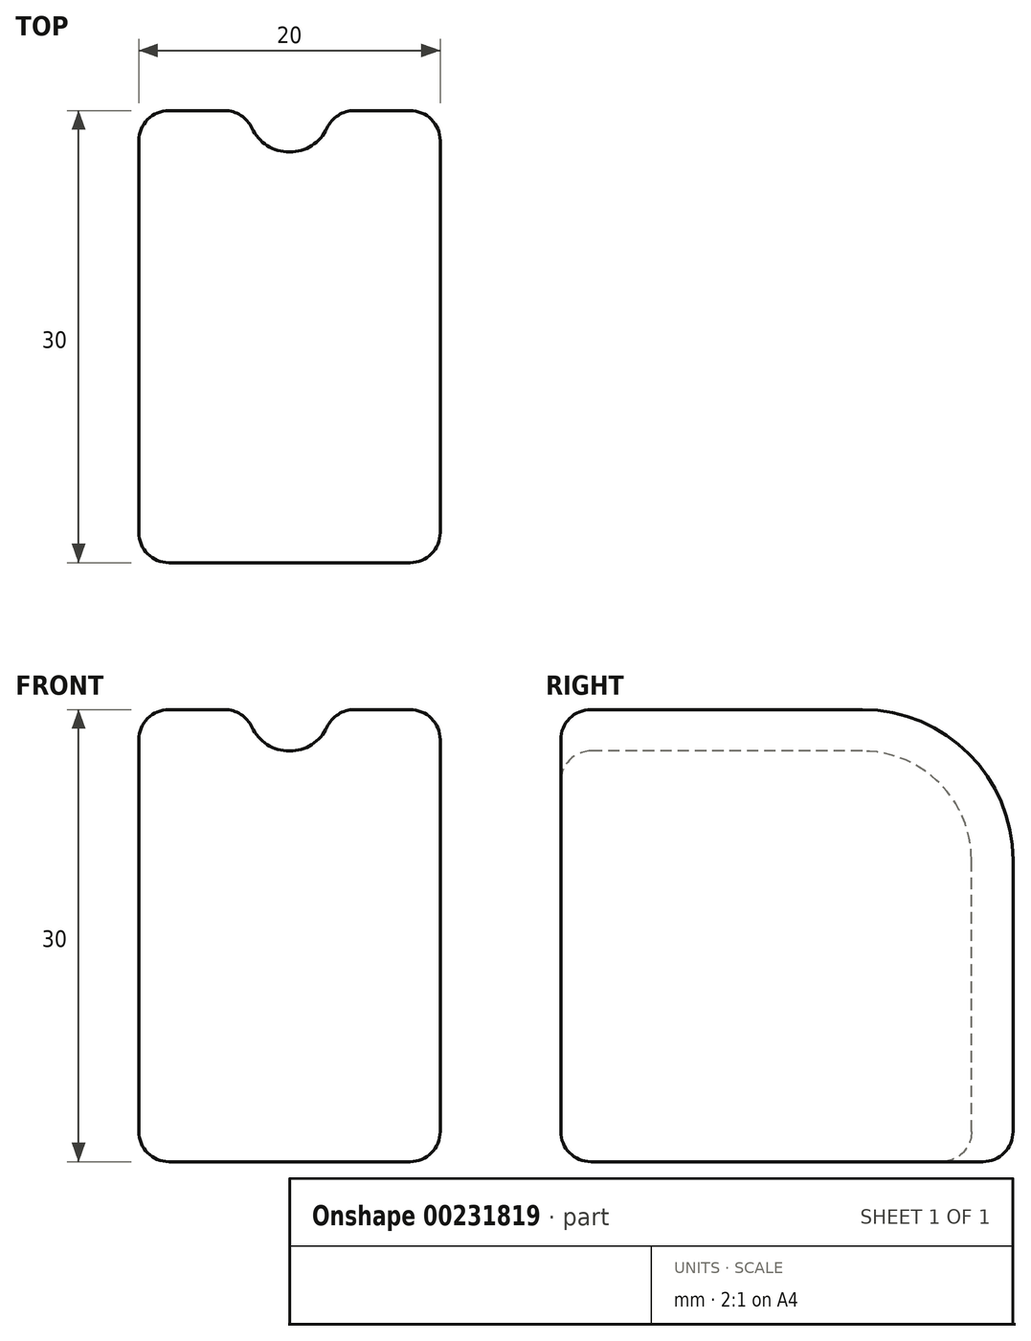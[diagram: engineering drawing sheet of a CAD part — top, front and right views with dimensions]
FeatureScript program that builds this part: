
annotation { "Feature Type Name" : "Feature", "Feature Type Description" : "" }
export const myFeature = defineFeature(function(context is Context, id is Id, definition is map)
    precondition{}
    {
        {
            var Q0;
            Q0=qCreatedBy(makeId("Top.planeOp"),FACE);
            var sketch = newSketch(context, id + "F0", { "sketchPlane" : qUnion([Q0])});
            skCircle(sketch, "E0", {"center": v(0, 0) * mm, "radius": 9.5 * mm});
            skCircle(sketch, "E1", {"center": v(0, 0) * mm, "radius": 8 * mm});
            skSolve(sketch);
        }
        {
            var Q0;
            Q0 = qSketchRegion(id + "F0", true);
            extrude(context, id + "F1", {"entities" : qUnion([Q0]), "depth" : 150 * mm});
        }
        {
            var Q0;
            Q0=makeQuery(id+"F1.opExtrude","SWEPT_BODY",BODY,{"disambiguationData":[OSD([sQuery(id+"F0.wireOp",EDGE,"E0"),sQuery(id+"F0.wireOp",EDGE,"E1")])]});
            deleteBodies(context, id + "F2", {"entities" : qUnion([Q0])});
        }
        {
            var Q0;
            Q0=qCreatedBy(makeId("Top.planeOp"),FACE);
            var sketch = newSketch(context, id + "F3", { "sketchPlane" : qUnion([Q0])});
            skLineSegment(sketch, "E2.bottom", {"start": v(10, 15) * mm, "end": v(-10, 15) * mm});
            skLineSegment(sketch, "E2.top", {"start": v(10, -15) * mm, "end": v(-10, -15) * mm});
            skLineSegment(sketch, "E2.left", {"start": v(10, 15) * mm, "end": v(10, -15) * mm});
            skLineSegment(sketch, "E2.right", {"start": v(-10, 15) * mm, "end": v(-10, -15) * mm});
            skPoint(sketch, "E2.middle", {"position": v(0, 0) * mm});
            skSolve(sketch);
        }
        {
            var Q0;
            Q0 = qSketchRegion(id + "F3", true);
            extrude(context, id + "F4", {"entities" : qUnion([Q0]), "depth" : 30 * mm});
        }
        {
            var Q0;
            Q0=makeQuery(id+"F4.opExtrude","CAP_EDGE",EDGE,{"disambiguationData":[OSD([sQuery(id+"F3.wireOp",EDGE,"E2.bottom")])],"isStart":false});
            fillet(context, id + "F5", {"entities" : qUnion([Q0]), "radius" : 10 * mm, "tangentPropagation" : true, "allowEdgeOverflow" : false});
        }
        {
            var Q0;
            Q0=qCreatedBy(makeId("Right.planeOp"),FACE);
            var sketch = newSketch(context, id + "F6", { "sketchPlane" : qUnion([Q0])});
            skLineSegment(sketch, "E3", {"start": v(15, 0) * mm, "end": v(15, 20) * mm});
            skLineSegment(sketch, "E4", {"start": v(-15.06, 30) * mm, "end": v(5, 30) * mm});
            skPoint(sketch, "E5.visualSharp", {"position": v(15, 30) * mm});
            skArc(sketch, "E5.filletArc", {"start": v(15, 20) * mm, "mid": v(12.07, 27.07) * mm, "end": v(5, 30) * mm});
            skSolve(sketch);
        }
        {
            var Q0;
            Q0=makeQuery(id+"F4.opExtrude","CAP_FACE",FACE,{"disambiguationData":[OSD([sQuery(id+"F3.wireOp",EDGE,"E2.bottom"),sQuery(id+"F3.wireOp",EDGE,"E2.top"),sQuery(id+"F3.wireOp",EDGE,"E2.left"),sQuery(id+"F3.wireOp",EDGE,"E2.right")])],"isStart":true});
            var sketch = newSketch(context, id + "F7", { "sketchPlane" : qUnion([Q0])});
            skArc(sketch, "E6", {"start": v(2.75, -15) * mm, "mid": v(0, -12.25) * mm, "end": v(-2.75, -15) * mm});
            skLineSegment(sketch, "E7", {"start": v(2.75, -15) * mm, "end": v(-2.75, -15) * mm});
            skSolve(sketch);
        }
        {
            var Q0;
            Q0 = qSketchRegion(id + "F7", true);
            var Q1;
            Q1 = qConstructionFilter(qBodyType(qCreatedBy(id + "F7" ,EDGE), BodyType.WIRE), ConstructionObject.NO);
            var Q2;
            Q2=sQuery(id+"F6.wireOp",EDGE,"E3");
            var Q3;
            Q3=sQuery(id+"F6.wireOp",EDGE,"E5.filletArc");
            var Q4;
            Q4=sQuery(id+"F6.wireOp",EDGE,"E4");
            sweep(context, id + "F8", {"operationType" : NewBodyOperationType.REMOVE, "profiles" : qUnion([Q0]), "surfaceProfiles" : qUnion([Q1]), "path" : qUnion([Q2, Q3, Q4])});
        }
        {
            var Q0;
            Q0=makeQuery(id+"F8.boolean.opBoolean","COPY",FACE,{"derivedFrom":makeQuery(id+"F8.opSweep","SWEPT_FACE",FACE,{"disambiguationData":[OSD([sQuery(id+"F6.wireOp",EDGE,"E4"),sQuery(id+"F7.wireOp",EDGE,"E6")])]})});
            var Q1;
            Q1=makeQuery(id+"F8.boolean.opBoolean","COPY",FACE,{"derivedFrom":makeQuery(id+"F8.opSweep","SWEPT_FACE",FACE,{"disambiguationData":[OSD([sQuery(id+"F6.wireOp",EDGE,"E5.filletArc"),sQuery(id+"F7.wireOp",EDGE,"E6")])]})});
            var Q2;
            Q2=makeQuery(id+"F8.boolean.opBoolean","COPY",FACE,{"derivedFrom":makeQuery(id+"F8.opSweep","SWEPT_FACE",FACE,{"disambiguationData":[OSD([sQuery(id+"F6.wireOp",EDGE,"E3"),sQuery(id+"F7.wireOp",EDGE,"E6")])]})});
            var Q3;
            Q3=makeQuery(id+"F5.opFillet","BLEND_EDGE",EDGE,{"blendedFrom":[makeQuery(id+"F4.opExtrude","CAP_EDGE",EDGE,{"disambiguationData":[OSD([sQuery(id+"F3.wireOp",EDGE,"E2.bottom")])],"isStart":false}),makeQuery(id+"F4.opExtrude","SWEPT_FACE",FACE,{"disambiguationData":[OSD([sQuery(id+"F3.wireOp",EDGE,"E2.right")])]})],"blendedInto":[makeQuery(id+"F4.opExtrude","SWEPT_FACE",FACE,{"disambiguationData":[OSD([sQuery(id+"F3.wireOp",EDGE,"E2.right")])]})]});
            var Q4;
            Q4=makeQuery(id+"F5.opFillet","BLEND_EDGE",EDGE,{"blendedFrom":[makeQuery(id+"F4.opExtrude","CAP_EDGE",EDGE,{"disambiguationData":[OSD([sQuery(id+"F3.wireOp",EDGE,"E2.bottom")])],"isStart":false}),makeQuery(id+"F4.opExtrude","SWEPT_FACE",FACE,{"disambiguationData":[OSD([sQuery(id+"F3.wireOp",EDGE,"E2.left")])]})],"blendedInto":[makeQuery(id+"F4.opExtrude","SWEPT_FACE",FACE,{"disambiguationData":[OSD([sQuery(id+"F3.wireOp",EDGE,"E2.left")])]})]});
            var Q5;
            Q5=makeQuery(id+"F4.opExtrude","SWEPT_FACE",FACE,{"disambiguationData":[OSD([sQuery(id+"F3.wireOp",EDGE,"E2.left")])]});
            var Q6;
            Q6=makeQuery(id+"F4.opExtrude","SWEPT_FACE",FACE,{"disambiguationData":[OSD([sQuery(id+"F3.wireOp",EDGE,"E2.right")])]});
            var Q7;
            Q7=makeQuery(id+"F4.opExtrude","CAP_FACE",FACE,{"disambiguationData":[OSD([sQuery(id+"F3.wireOp",EDGE,"E2.bottom"),sQuery(id+"F3.wireOp",EDGE,"E2.top"),sQuery(id+"F3.wireOp",EDGE,"E2.left"),sQuery(id+"F3.wireOp",EDGE,"E2.right")])],"isStart":true});
            var Q8;
            Q8=makeQuery(id+"F4.opExtrude","SWEPT_FACE",FACE,{"disambiguationData":[OSD([sQuery(id+"F3.wireOp",EDGE,"E2.top")])]});
            fillet(context, id + "F9", {"entities" : qUnion([Q0, Q1, Q2, Q3, Q4, Q5, Q6, Q7, Q8]), "radius" : 2 * mm, "tangentPropagation" : true, "allowEdgeOverflow" : false});
        }
    });
